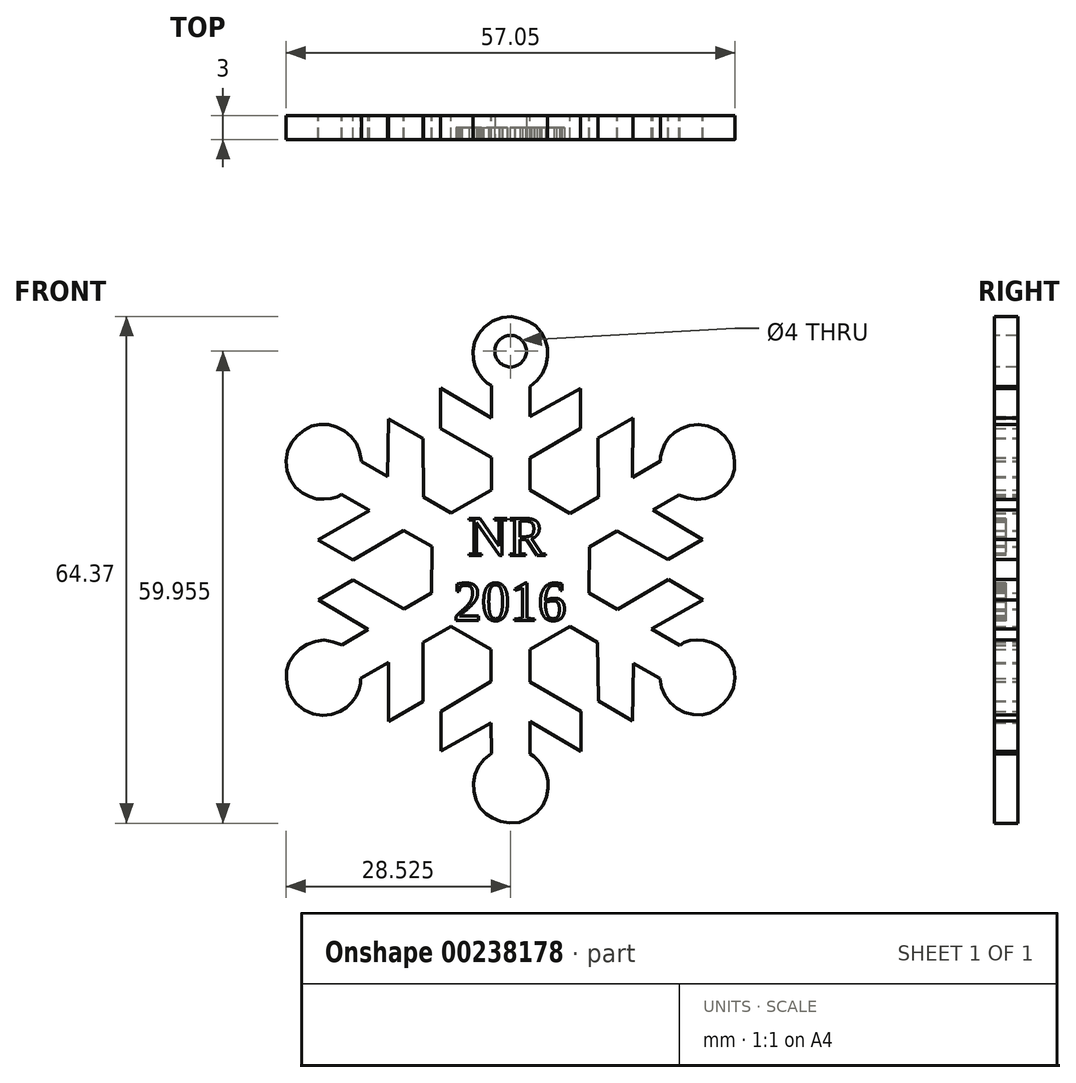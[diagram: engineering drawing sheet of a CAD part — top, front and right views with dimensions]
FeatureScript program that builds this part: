
annotation { "Feature Type Name" : "Feature", "Feature Type Description" : "" }
export const myFeature = defineFeature(function(context is Context, id is Id, definition is map)
    precondition{}
    {
        {
            var Q0;
            Q0=qCreatedBy(makeId("Front.planeOp"),FACE);
            var sketch = newSketch(context, id + "F0", { "sketchPlane" : qUnion([Q0])});
            skFitSpline(sketch, "E0", {"points": [v(37.24, 9.43) * mm, v(37.81, 9.11) * mm, v(38.63, 8.19) * mm, v(39.3, 6.99) * mm, v(39.56, 5.42) * mm, v(39.13, 3.37) * mm, v(37.49, 1.48) * mm, v(35, 0.65) * mm, v(32.8, 1.18) * mm, v(31.32, 2.12) * mm, v(30.3, 3.9) * mm, v(30.1, 5.9) * mm, v(30.72, 7.91) * mm, v(32.35, 9.53) * mm], "startDerivative": vector(12.25, -5.47) * mm, "endDerivative": vector(21.42, 17.4) * mm});
            skFitSpline(sketch, "E1", {"points": [v(32.35, 56.24) * mm, v(31.78, 56.56) * mm, v(30.95, 57.49) * mm, v(30.28, 58.69) * mm, v(30.03, 60.26) * mm, v(30.45, 62.3) * mm, v(32.1, 64.2) * mm, v(34.6, 65.02) * mm, v(36.8, 64.5) * mm, v(38.26, 63.55) * mm, v(39.29, 61.78) * mm, v(39.49, 59.78) * mm, v(38.86, 57.76) * mm, v(37.24, 56.14) * mm], "startDerivative": vector(-12.25, 5.47) * mm, "endDerivative": vector(-21.42, -17.4) * mm});
            skLineSegment(sketch, "E2", {"start": v(32.35, 56.24) * mm, "end": v(32.35, 52.12) * mm});
            skLineSegment(sketch, "E3", {"start": v(32.35, 52.12) * mm, "end": v(25.87, 55.93) * mm});
            skLineSegment(sketch, "E4", {"start": v(25.87, 55.93) * mm, "end": v(25.87, 50.81) * mm});
            skLineSegment(sketch, "E5", {"start": v(25.87, 50.81) * mm, "end": v(32.35, 47.1) * mm});
            skLineSegment(sketch, "E6", {"start": v(32.35, 47.1) * mm, "end": v(32.35, 42.96) * mm});
            skLineSegment(sketch, "E7", {"start": v(37.27, 42.98) * mm, "end": v(37.27, 47.04) * mm});
            skLineSegment(sketch, "E8", {"start": v(37.27, 47.04) * mm, "end": v(43.65, 50.81) * mm});
            skLineSegment(sketch, "E9", {"start": v(43.65, 50.81) * mm, "end": v(43.65, 55.86) * mm});
            skLineSegment(sketch, "E10", {"start": v(43.65, 55.86) * mm, "end": v(37.27, 52.3) * mm});
            skLineSegment(sketch, "E11", {"start": v(37.27, 52.3) * mm, "end": v(37.24, 56.14) * mm});
            skLineSegment(sketch, "E12", {"start": v(27.25, 40.05) * mm, "end": v(32.35, 42.96) * mm});
            skLineSegment(sketch, "E13.1.0", {"start": v(21.21, 37.86) * mm, "end": v(24.8, 35.78) * mm});
            skLineSegment(sketch, "E13.1.1", {"start": v(27.25, 40.05) * mm, "end": v(23.73, 42.08) * mm});
            skLineSegment(sketch, "E13.1.2", {"start": v(24.78, 29.9) * mm, "end": v(24.8, 35.78) * mm});
            skLineSegment(sketch, "E13.1.3", {"start": v(14.76, 34.1) * mm, "end": v(21.21, 37.86) * mm});
            skLineSegment(sketch, "E13.1.4", {"start": v(23.73, 42.08) * mm, "end": v(23.66, 49.5) * mm});
            skLineSegment(sketch, "E13.1.5", {"start": v(23.66, 49.5) * mm, "end": v(19.29, 52.02) * mm});
            skLineSegment(sketch, "E13.1.6", {"start": v(19.29, 52.02) * mm, "end": v(19.18, 44.7) * mm});
            skLineSegment(sketch, "E13.1.7", {"start": v(19.18, 44.7) * mm, "end": v(15.84, 46.6) * mm});
            skLineSegment(sketch, "E13.1.8", {"start": v(13.3, 42.42) * mm, "end": v(16.87, 40.36) * mm});
            skLineSegment(sketch, "E13.1.9", {"start": v(16.87, 40.36) * mm, "end": v(10.33, 36.65) * mm});
            skLineSegment(sketch, "E13.1.10", {"start": v(10.33, 36.65) * mm, "end": v(14.76, 34.1) * mm});
            skLineSegment(sketch, "E13.2.0", {"start": v(23.66, 23.59) * mm, "end": v(27.25, 25.66) * mm});
            skLineSegment(sketch, "E13.2.1", {"start": v(24.78, 29.9) * mm, "end": v(21.26, 27.88) * mm});
            skLineSegment(sketch, "E13.2.2", {"start": v(32.32, 22.7) * mm, "end": v(27.25, 25.66) * mm});
            skLineSegment(sketch, "E13.2.3", {"start": v(23.7, 16.12) * mm, "end": v(23.66, 23.59) * mm});
            skLineSegment(sketch, "E13.2.4", {"start": v(21.26, 27.88) * mm, "end": v(14.8, 31.52) * mm});
            skLineSegment(sketch, "E13.2.5", {"start": v(14.8, 31.52) * mm, "end": v(10.43, 29) * mm});
            skLineSegment(sketch, "E13.2.6", {"start": v(10.43, 29) * mm, "end": v(16.7, 25.25) * mm});
            skLineSegment(sketch, "E13.2.7", {"start": v(16.7, 25.25) * mm, "end": v(13.39, 23.3) * mm});
            skLineSegment(sketch, "E13.2.8", {"start": v(15.75, 19.02) * mm, "end": v(19.32, 21.08) * mm});
            skLineSegment(sketch, "E13.2.9", {"start": v(19.32, 21.08) * mm, "end": v(19.26, 13.56) * mm});
            skLineSegment(sketch, "E13.2.10", {"start": v(19.26, 13.56) * mm, "end": v(23.7, 16.12) * mm});
            skLineSegment(sketch, "E13.3.0", {"start": v(37.24, 18.57) * mm, "end": v(37.24, 22.71) * mm});
            skLineSegment(sketch, "E13.3.1", {"start": v(32.32, 22.7) * mm, "end": v(32.32, 18.64) * mm});
            skLineSegment(sketch, "E13.3.2", {"start": v(42.34, 25.63) * mm, "end": v(37.24, 22.71) * mm});
            skLineSegment(sketch, "E13.3.3", {"start": v(43.72, 14.86) * mm, "end": v(37.24, 18.57) * mm});
            skLineSegment(sketch, "E13.3.4", {"start": v(32.32, 18.64) * mm, "end": v(25.93, 14.86) * mm});
            skLineSegment(sketch, "E13.3.5", {"start": v(25.93, 14.86) * mm, "end": v(25.93, 9.82) * mm});
            skLineSegment(sketch, "E13.3.6", {"start": v(25.93, 9.82) * mm, "end": v(32.32, 13.38) * mm});
            skLineSegment(sketch, "E13.3.7", {"start": v(32.32, 13.38) * mm, "end": v(32.35, 9.53) * mm});
            skLineSegment(sketch, "E13.3.8", {"start": v(37.24, 9.43) * mm, "end": v(37.24, 13.56) * mm});
            skLineSegment(sketch, "E13.3.9", {"start": v(37.24, 13.56) * mm, "end": v(43.72, 9.75) * mm});
            skLineSegment(sketch, "E13.3.10", {"start": v(43.72, 9.75) * mm, "end": v(43.72, 14.86) * mm});
            skLineSegment(sketch, "E13.4.0", {"start": v(48.37, 27.82) * mm, "end": v(44.78, 29.9) * mm});
            skLineSegment(sketch, "E13.4.1", {"start": v(42.34, 25.63) * mm, "end": v(45.85, 23.6) * mm});
            skLineSegment(sketch, "E13.4.2", {"start": v(44.81, 35.77) * mm, "end": v(44.78, 29.9) * mm});
            skLineSegment(sketch, "E13.4.3", {"start": v(54.82, 31.58) * mm, "end": v(48.37, 27.82) * mm});
            skLineSegment(sketch, "E13.4.4", {"start": v(45.85, 23.6) * mm, "end": v(45.93, 16.18) * mm});
            skLineSegment(sketch, "E13.4.5", {"start": v(45.93, 16.18) * mm, "end": v(50.3, 13.65) * mm});
            skLineSegment(sketch, "E13.4.6", {"start": v(50.3, 13.65) * mm, "end": v(50.4, 20.97) * mm});
            skLineSegment(sketch, "E13.4.7", {"start": v(50.4, 20.97) * mm, "end": v(53.75, 19.07) * mm});
            skLineSegment(sketch, "E13.4.8", {"start": v(56.28, 23.25) * mm, "end": v(52.71, 25.31) * mm});
            skLineSegment(sketch, "E13.4.9", {"start": v(52.71, 25.31) * mm, "end": v(59.25, 29.02) * mm});
            skLineSegment(sketch, "E13.4.10", {"start": v(59.25, 29.02) * mm, "end": v(54.82, 31.58) * mm});
            skLineSegment(sketch, "E13.5.0", {"start": v(45.93, 42.09) * mm, "end": v(42.34, 40.02) * mm});
            skLineSegment(sketch, "E13.5.1", {"start": v(44.81, 35.77) * mm, "end": v(48.33, 37.8) * mm});
            skLineSegment(sketch, "E13.5.2", {"start": v(37.27, 42.98) * mm, "end": v(42.34, 40.02) * mm});
            skLineSegment(sketch, "E13.5.3", {"start": v(45.9, 49.55) * mm, "end": v(45.93, 42.09) * mm});
            skLineSegment(sketch, "E13.5.4", {"start": v(48.33, 37.8) * mm, "end": v(54.79, 34.15) * mm});
            skLineSegment(sketch, "E13.5.5", {"start": v(54.79, 34.15) * mm, "end": v(59.16, 36.67) * mm});
            skLineSegment(sketch, "E13.5.6", {"start": v(59.16, 36.67) * mm, "end": v(52.88, 40.42) * mm});
            skLineSegment(sketch, "E13.5.7", {"start": v(52.88, 40.42) * mm, "end": v(56.2, 42.37) * mm});
            skLineSegment(sketch, "E13.5.8", {"start": v(53.84, 46.66) * mm, "end": v(50.27, 44.6) * mm});
            skLineSegment(sketch, "E13.5.9", {"start": v(50.27, 44.6) * mm, "end": v(50.33, 52.11) * mm});
            skLineSegment(sketch, "E13.5.10", {"start": v(50.33, 52.11) * mm, "end": v(45.9, 49.55) * mm});
            skPoint(sketch, "E13.center", {"position": v(34.8, 32.84) * mm});
            skFitSpline(sketch, "E14", {"points": [v(15.75, 19.02) * mm, v(15.74, 18.36) * mm, v(15.35, 17.18) * mm, v(14.65, 16) * mm, v(13.41, 15) * mm, v(11.43, 14.34) * mm, v(8.96, 14.82) * mm, v(7, 16.57) * mm, v(6.36, 18.74) * mm, v(6.44, 20.48) * mm, v(7.46, 22.26) * mm, v(9.1, 23.43) * mm, v(11.16, 23.9) * mm, v(13.39, 23.3) * mm], "startDerivative": vector(1.38, -13.34) * mm, "endDerivative": vector(25.78, -9.85) * mm});
            skFitSpline(sketch, "E15", {"points": [v(56.28, 23.25) * mm, v(56.86, 23.64) * mm, v(58.07, 23.9) * mm, v(59.44, 23.88) * mm, v(60.93, 23.3) * mm, v(62.49, 21.91) * mm, v(63.3, 19.54) * mm, v(62.77, 16.97) * mm, v(61.22, 15.33) * mm, v(59.66, 14.53) * mm, v(57.62, 14.53) * mm, v(55.8, 15.35) * mm, v(54.35, 16.9) * mm, v(53.75, 19.07) * mm], "startDerivative": vector(10.86, 7.87) * mm, "endDerivative": vector(-4.36, 27.26) * mm});
            skFitSpline(sketch, "E16", {"points": [v(13.3, 42.42) * mm, v(12.73, 42.1) * mm, v(11.52, 41.85) * mm, v(10.14, 41.86) * mm, v(8.66, 42.43) * mm, v(7.1, 43.82) * mm, v(6.28, 46.2) * mm, v(6.81, 48.77) * mm, v(8.37, 50.4) * mm, v(9.92, 51.21) * mm, v(11.97, 51.21) * mm, v(13.8, 50.39) * mm, v(15.24, 48.83) * mm, v(15.84, 46.6) * mm], "startDerivative": vector(-10.86, -7.87) * mm, "endDerivative": vector(4.36, -27.26) * mm});
            skFitSpline(sketch, "E17", {"points": [v(53.84, 46.66) * mm, v(53.84, 47.28) * mm, v(54.23, 48.46) * mm, v(54.93, 49.64) * mm, v(56.16, 50.64) * mm, v(58.15, 51.3) * mm, v(60.61, 50.82) * mm, v(62.57, 49.07) * mm, v(63.22, 46.9) * mm, v(63.13, 45.16) * mm, v(62.11, 43.39) * mm, v(60.48, 42.21) * mm, v(58.42, 41.74) * mm, v(56.2, 42.37) * mm], "startDerivative": vector(-1.38, 13.34) * mm, "endDerivative": vector(-25.78, 9.85) * mm});
            skSolve(sketch);
        }
        {
            var Q0;
            Q0=makeQuery(id+"F0.imprint","IMPRINT",FACE,{"disambiguationData":[TD([[makeQuery(id+"F0.imprint","IMPRINT",EDGE,{"derivedFrom":sQuery(id+"F0.wireOp",EDGE,"E0")}),-1.0]])]});
            extrude(context, id + "F1", {"entities" : qUnion([Q0]), "depth" : 3 * mm});
        }
        {
            var Q0;
            Q0=makeQuery(id+"F1.opExtrude","CAP_FACE",FACE,{"disambiguationData":[OSD([sQuery(id+"F0.wireOp",EDGE,"E0"),sQuery(id+"F0.wireOp",EDGE,"E1"),sQuery(id+"F0.wireOp",EDGE,"E2"),sQuery(id+"F0.wireOp",EDGE,"E3"),sQuery(id+"F0.wireOp",EDGE,"E4"),sQuery(id+"F0.wireOp",EDGE,"E5"),sQuery(id+"F0.wireOp",EDGE,"E6"),sQuery(id+"F0.wireOp",EDGE,"E7"),sQuery(id+"F0.wireOp",EDGE,"E8"),sQuery(id+"F0.wireOp",EDGE,"E9"),sQuery(id+"F0.wireOp",EDGE,"E10"),sQuery(id+"F0.wireOp",EDGE,"E11"),sQuery(id+"F0.wireOp",EDGE,"E12"),sQuery(id+"F0.wireOp",EDGE,"E13.1.0"),sQuery(id+"F0.wireOp",EDGE,"E13.1.1"),sQuery(id+"F0.wireOp",EDGE,"E13.1.2"),sQuery(id+"F0.wireOp",EDGE,"E13.1.3"),sQuery(id+"F0.wireOp",EDGE,"E13.1.4"),sQuery(id+"F0.wireOp",EDGE,"E13.1.5"),sQuery(id+"F0.wireOp",EDGE,"E13.1.6"),sQuery(id+"F0.wireOp",EDGE,"E13.1.7"),sQuery(id+"F0.wireOp",EDGE,"E13.1.8"),sQuery(id+"F0.wireOp",EDGE,"E13.1.9"),sQuery(id+"F0.wireOp",EDGE,"E13.1.10"),sQuery(id+"F0.wireOp",EDGE,"E13.2.0"),sQuery(id+"F0.wireOp",EDGE,"E13.2.1"),sQuery(id+"F0.wireOp",EDGE,"E13.2.2"),sQuery(id+"F0.wireOp",EDGE,"E13.2.3"),sQuery(id+"F0.wireOp",EDGE,"E13.2.4"),sQuery(id+"F0.wireOp",EDGE,"E13.2.5"),sQuery(id+"F0.wireOp",EDGE,"E13.2.6"),sQuery(id+"F0.wireOp",EDGE,"E13.2.7"),sQuery(id+"F0.wireOp",EDGE,"E13.2.8"),sQuery(id+"F0.wireOp",EDGE,"E13.2.9"),sQuery(id+"F0.wireOp",EDGE,"E13.2.10"),sQuery(id+"F0.wireOp",EDGE,"E13.3.0"),sQuery(id+"F0.wireOp",EDGE,"E13.3.1"),sQuery(id+"F0.wireOp",EDGE,"E13.3.2"),sQuery(id+"F0.wireOp",EDGE,"E13.3.3"),sQuery(id+"F0.wireOp",EDGE,"E13.3.4"),sQuery(id+"F0.wireOp",EDGE,"E13.3.5"),sQuery(id+"F0.wireOp",EDGE,"E13.3.6"),sQuery(id+"F0.wireOp",EDGE,"E13.3.7"),sQuery(id+"F0.wireOp",EDGE,"E13.3.8"),sQuery(id+"F0.wireOp",EDGE,"E13.3.9"),sQuery(id+"F0.wireOp",EDGE,"E13.3.10"),sQuery(id+"F0.wireOp",EDGE,"E13.4.0"),sQuery(id+"F0.wireOp",EDGE,"E13.4.1"),sQuery(id+"F0.wireOp",EDGE,"E13.4.2"),sQuery(id+"F0.wireOp",EDGE,"E13.4.3"),sQuery(id+"F0.wireOp",EDGE,"E13.4.4"),sQuery(id+"F0.wireOp",EDGE,"E13.4.5"),sQuery(id+"F0.wireOp",EDGE,"E13.4.6"),sQuery(id+"F0.wireOp",EDGE,"E13.4.7"),sQuery(id+"F0.wireOp",EDGE,"E13.4.8"),sQuery(id+"F0.wireOp",EDGE,"E13.4.9"),sQuery(id+"F0.wireOp",EDGE,"E13.4.10"),sQuery(id+"F0.wireOp",EDGE,"E13.5.0"),sQuery(id+"F0.wireOp",EDGE,"E13.5.1"),sQuery(id+"F0.wireOp",EDGE,"E13.5.2"),sQuery(id+"F0.wireOp",EDGE,"E13.5.3"),sQuery(id+"F0.wireOp",EDGE,"E13.5.4"),sQuery(id+"F0.wireOp",EDGE,"E13.5.5"),sQuery(id+"F0.wireOp",EDGE,"E13.5.6"),sQuery(id+"F0.wireOp",EDGE,"E13.5.7"),sQuery(id+"F0.wireOp",EDGE,"E13.5.8"),sQuery(id+"F0.wireOp",EDGE,"E13.5.9"),sQuery(id+"F0.wireOp",EDGE,"E13.5.10"),sQuery(id+"F0.wireOp",EDGE,"E14"),sQuery(id+"F0.wireOp",EDGE,"E15"),sQuery(id+"F0.wireOp",EDGE,"E16"),sQuery(id+"F0.wireOp",EDGE,"E17")])],"isStart":false});
            var sketch = newSketch(context, id + "F2", { "sketchPlane" : qUnion([Q0])});
            skCircle(sketch, "E18", {"center": v(34.8, 60.6) * mm, "radius": 2 * mm});
            skSolve(sketch);
        }
        {
            var Q0;
            Q0=sQuery(id+"F2.wireOp",VERTEX,"E18.center");
            var Q1;
            Q1=makeQuery(id+"F1.opExtrude","SWEPT_BODY",BODY,{"disambiguationData":[OSD([sQuery(id+"F0.wireOp",EDGE,"E0"),sQuery(id+"F0.wireOp",EDGE,"E1"),sQuery(id+"F0.wireOp",EDGE,"E2"),sQuery(id+"F0.wireOp",EDGE,"E3"),sQuery(id+"F0.wireOp",EDGE,"E4"),sQuery(id+"F0.wireOp",EDGE,"E5"),sQuery(id+"F0.wireOp",EDGE,"E6"),sQuery(id+"F0.wireOp",EDGE,"E7"),sQuery(id+"F0.wireOp",EDGE,"E8"),sQuery(id+"F0.wireOp",EDGE,"E9"),sQuery(id+"F0.wireOp",EDGE,"E10"),sQuery(id+"F0.wireOp",EDGE,"E11"),sQuery(id+"F0.wireOp",EDGE,"E12"),sQuery(id+"F0.wireOp",EDGE,"E13.1.0"),sQuery(id+"F0.wireOp",EDGE,"E13.1.1"),sQuery(id+"F0.wireOp",EDGE,"E13.1.2"),sQuery(id+"F0.wireOp",EDGE,"E13.1.3"),sQuery(id+"F0.wireOp",EDGE,"E13.1.4"),sQuery(id+"F0.wireOp",EDGE,"E13.1.5"),sQuery(id+"F0.wireOp",EDGE,"E13.1.6"),sQuery(id+"F0.wireOp",EDGE,"E13.1.7"),sQuery(id+"F0.wireOp",EDGE,"E13.1.8"),sQuery(id+"F0.wireOp",EDGE,"E13.1.9"),sQuery(id+"F0.wireOp",EDGE,"E13.1.10"),sQuery(id+"F0.wireOp",EDGE,"E13.2.0"),sQuery(id+"F0.wireOp",EDGE,"E13.2.1"),sQuery(id+"F0.wireOp",EDGE,"E13.2.2"),sQuery(id+"F0.wireOp",EDGE,"E13.2.3"),sQuery(id+"F0.wireOp",EDGE,"E13.2.4"),sQuery(id+"F0.wireOp",EDGE,"E13.2.5"),sQuery(id+"F0.wireOp",EDGE,"E13.2.6"),sQuery(id+"F0.wireOp",EDGE,"E13.2.7"),sQuery(id+"F0.wireOp",EDGE,"E13.2.8"),sQuery(id+"F0.wireOp",EDGE,"E13.2.9"),sQuery(id+"F0.wireOp",EDGE,"E13.2.10"),sQuery(id+"F0.wireOp",EDGE,"E13.3.0"),sQuery(id+"F0.wireOp",EDGE,"E13.3.1"),sQuery(id+"F0.wireOp",EDGE,"E13.3.2"),sQuery(id+"F0.wireOp",EDGE,"E13.3.3"),sQuery(id+"F0.wireOp",EDGE,"E13.3.4"),sQuery(id+"F0.wireOp",EDGE,"E13.3.5"),sQuery(id+"F0.wireOp",EDGE,"E13.3.6"),sQuery(id+"F0.wireOp",EDGE,"E13.3.7"),sQuery(id+"F0.wireOp",EDGE,"E13.3.8"),sQuery(id+"F0.wireOp",EDGE,"E13.3.9"),sQuery(id+"F0.wireOp",EDGE,"E13.3.10"),sQuery(id+"F0.wireOp",EDGE,"E13.4.0"),sQuery(id+"F0.wireOp",EDGE,"E13.4.1"),sQuery(id+"F0.wireOp",EDGE,"E13.4.2"),sQuery(id+"F0.wireOp",EDGE,"E13.4.3"),sQuery(id+"F0.wireOp",EDGE,"E13.4.4"),sQuery(id+"F0.wireOp",EDGE,"E13.4.5"),sQuery(id+"F0.wireOp",EDGE,"E13.4.6"),sQuery(id+"F0.wireOp",EDGE,"E13.4.7"),sQuery(id+"F0.wireOp",EDGE,"E13.4.8"),sQuery(id+"F0.wireOp",EDGE,"E13.4.9"),sQuery(id+"F0.wireOp",EDGE,"E13.4.10"),sQuery(id+"F0.wireOp",EDGE,"E13.5.0"),sQuery(id+"F0.wireOp",EDGE,"E13.5.1"),sQuery(id+"F0.wireOp",EDGE,"E13.5.2"),sQuery(id+"F0.wireOp",EDGE,"E13.5.3"),sQuery(id+"F0.wireOp",EDGE,"E13.5.4"),sQuery(id+"F0.wireOp",EDGE,"E13.5.5"),sQuery(id+"F0.wireOp",EDGE,"E13.5.6"),sQuery(id+"F0.wireOp",EDGE,"E13.5.7"),sQuery(id+"F0.wireOp",EDGE,"E13.5.8"),sQuery(id+"F0.wireOp",EDGE,"E13.5.9"),sQuery(id+"F0.wireOp",EDGE,"E13.5.10"),sQuery(id+"F0.wireOp",EDGE,"E14"),sQuery(id+"F0.wireOp",EDGE,"E15"),sQuery(id+"F0.wireOp",EDGE,"E16"),sQuery(id+"F0.wireOp",EDGE,"E17")])]});
            hole(context, id + "F3", {"style" : HoleStyle.SIMPLE, "endStyle" : HoleEndStyle.THROUGH, "holeDiameter" : 4 * mm, "isTappedThrough" : true, "tappedDepth" : 12 * mm, "tapClearance" : 3, "locations" : qUnion([Q0]), "scope" : qUnion([Q1])});
        }
        {
            var Q0;
            Q0=makeQuery(id+"F1.opExtrude","CAP_FACE",FACE,{"disambiguationData":[OSD([sQuery(id+"F0.wireOp",EDGE,"E0"),sQuery(id+"F0.wireOp",EDGE,"E1"),sQuery(id+"F0.wireOp",EDGE,"E2"),sQuery(id+"F0.wireOp",EDGE,"E3"),sQuery(id+"F0.wireOp",EDGE,"E4"),sQuery(id+"F0.wireOp",EDGE,"E5"),sQuery(id+"F0.wireOp",EDGE,"E6"),sQuery(id+"F0.wireOp",EDGE,"E7"),sQuery(id+"F0.wireOp",EDGE,"E8"),sQuery(id+"F0.wireOp",EDGE,"E9"),sQuery(id+"F0.wireOp",EDGE,"E10"),sQuery(id+"F0.wireOp",EDGE,"E11"),sQuery(id+"F0.wireOp",EDGE,"E12"),sQuery(id+"F0.wireOp",EDGE,"E13.1.0"),sQuery(id+"F0.wireOp",EDGE,"E13.1.1"),sQuery(id+"F0.wireOp",EDGE,"E13.1.2"),sQuery(id+"F0.wireOp",EDGE,"E13.1.3"),sQuery(id+"F0.wireOp",EDGE,"E13.1.4"),sQuery(id+"F0.wireOp",EDGE,"E13.1.5"),sQuery(id+"F0.wireOp",EDGE,"E13.1.6"),sQuery(id+"F0.wireOp",EDGE,"E13.1.7"),sQuery(id+"F0.wireOp",EDGE,"E13.1.8"),sQuery(id+"F0.wireOp",EDGE,"E13.1.9"),sQuery(id+"F0.wireOp",EDGE,"E13.1.10"),sQuery(id+"F0.wireOp",EDGE,"E13.2.0"),sQuery(id+"F0.wireOp",EDGE,"E13.2.1"),sQuery(id+"F0.wireOp",EDGE,"E13.2.2"),sQuery(id+"F0.wireOp",EDGE,"E13.2.3"),sQuery(id+"F0.wireOp",EDGE,"E13.2.4"),sQuery(id+"F0.wireOp",EDGE,"E13.2.5"),sQuery(id+"F0.wireOp",EDGE,"E13.2.6"),sQuery(id+"F0.wireOp",EDGE,"E13.2.7"),sQuery(id+"F0.wireOp",EDGE,"E13.2.8"),sQuery(id+"F0.wireOp",EDGE,"E13.2.9"),sQuery(id+"F0.wireOp",EDGE,"E13.2.10"),sQuery(id+"F0.wireOp",EDGE,"E13.3.0"),sQuery(id+"F0.wireOp",EDGE,"E13.3.1"),sQuery(id+"F0.wireOp",EDGE,"E13.3.2"),sQuery(id+"F0.wireOp",EDGE,"E13.3.3"),sQuery(id+"F0.wireOp",EDGE,"E13.3.4"),sQuery(id+"F0.wireOp",EDGE,"E13.3.5"),sQuery(id+"F0.wireOp",EDGE,"E13.3.6"),sQuery(id+"F0.wireOp",EDGE,"E13.3.7"),sQuery(id+"F0.wireOp",EDGE,"E13.3.8"),sQuery(id+"F0.wireOp",EDGE,"E13.3.9"),sQuery(id+"F0.wireOp",EDGE,"E13.3.10"),sQuery(id+"F0.wireOp",EDGE,"E13.4.0"),sQuery(id+"F0.wireOp",EDGE,"E13.4.1"),sQuery(id+"F0.wireOp",EDGE,"E13.4.2"),sQuery(id+"F0.wireOp",EDGE,"E13.4.3"),sQuery(id+"F0.wireOp",EDGE,"E13.4.4"),sQuery(id+"F0.wireOp",EDGE,"E13.4.5"),sQuery(id+"F0.wireOp",EDGE,"E13.4.6"),sQuery(id+"F0.wireOp",EDGE,"E13.4.7"),sQuery(id+"F0.wireOp",EDGE,"E13.4.8"),sQuery(id+"F0.wireOp",EDGE,"E13.4.9"),sQuery(id+"F0.wireOp",EDGE,"E13.4.10"),sQuery(id+"F0.wireOp",EDGE,"E13.5.0"),sQuery(id+"F0.wireOp",EDGE,"E13.5.1"),sQuery(id+"F0.wireOp",EDGE,"E13.5.2"),sQuery(id+"F0.wireOp",EDGE,"E13.5.3"),sQuery(id+"F0.wireOp",EDGE,"E13.5.4"),sQuery(id+"F0.wireOp",EDGE,"E13.5.5"),sQuery(id+"F0.wireOp",EDGE,"E13.5.6"),sQuery(id+"F0.wireOp",EDGE,"E13.5.7"),sQuery(id+"F0.wireOp",EDGE,"E13.5.8"),sQuery(id+"F0.wireOp",EDGE,"E13.5.9"),sQuery(id+"F0.wireOp",EDGE,"E13.5.10"),sQuery(id+"F0.wireOp",EDGE,"E14"),sQuery(id+"F0.wireOp",EDGE,"E15"),sQuery(id+"F0.wireOp",EDGE,"E16"),sQuery(id+"F0.wireOp",EDGE,"E17")])],"isStart":false});
            var sketch = newSketch(context, id + "F4", { "sketchPlane" : qUnion([Q0])});
            skPoint(sketch, "E19", {"position": v(34.84, 32.8) * mm});
            skText(sketch, "E20", { "text": " NR\n2016", "fontName": "Tinos-Regular.ttf"});
            const initialGuessF4  = {"E20": [0.02752, 0.03466, 1, 0, 0.00516]};
            skSetInitialGuess(sketch, initialGuessF4);
            skSolve(sketch);
        }
        {
            var Q0;
            Q0=makeQuery(id+"F4.imprint","IMPRINT",FACE,{"disambiguationData":[TD([[makeQuery(id+"F4.imprint","IMPRINT",EDGE,{"derivedFrom":sQuery(id+"F4.wireOp",EDGE,"E20.sketch_text.stroke-0")}),-1.0]])]});
            var Q1;
            Q1=makeQuery(id+"F4.imprint","IMPRINT",FACE,{"disambiguationData":[TD([[makeQuery(id+"F4.imprint","IMPRINT",EDGE,{"derivedFrom":sQuery(id+"F4.wireOp",EDGE,"E20.sketch_text.stroke-22")}),-1.0]])]});
            var Q2;
            Q2=makeQuery(id+"F4.imprint","IMPRINT",FACE,{"disambiguationData":[TD([[makeQuery(id+"F4.imprint","IMPRINT",EDGE,{"derivedFrom":sQuery(id+"F4.wireOp",EDGE,"E20.sketch_text.stroke-37")}),-1.0]])]});
            var Q3;
            Q3=makeQuery(id+"F4.imprint","IMPRINT",FACE,{"disambiguationData":[TD([[makeQuery(id+"F4.imprint","IMPRINT",EDGE,{"derivedFrom":sQuery(id+"F4.wireOp",EDGE,"E20.sketch_text.stroke-48")}),-1.0]])]});
            var Q4;
            Q4=makeQuery(id+"F4.imprint","IMPRINT",FACE,{"disambiguationData":[TD([[makeQuery(id+"F4.imprint","IMPRINT",EDGE,{"derivedFrom":sQuery(id+"F4.wireOp",EDGE,"E20.sketch_text.stroke-49")}),-1.0]])]});
            var Q5;
            Q5=makeQuery(id+"F4.imprint","IMPRINT",FACE,{"disambiguationData":[TD([[makeQuery(id+"F4.imprint","IMPRINT",EDGE,{"derivedFrom":sQuery(id+"F4.wireOp",EDGE,"E20.sketch_text.stroke-71")}),-1.0]])]});
            var Q6;
            Q6=makeQuery(id+"F4.imprint","IMPRINT",FACE,{"disambiguationData":[TD([[makeQuery(id+"F4.imprint","IMPRINT",EDGE,{"derivedFrom":sQuery(id+"F4.wireOp",EDGE,"E20.sketch_text.stroke-86")}),-1.0]])]});
            var Q7;
            Q7=makeQuery(id+"F4.imprint","IMPRINT",FACE,{"disambiguationData":[TD([[makeQuery(id+"F4.imprint","IMPRINT",EDGE,{"derivedFrom":sQuery(id+"F4.wireOp",EDGE,"E20.sketch_text.stroke-97")}),-1.0]])]});
            extrude(context, id + "F5", {"entities" : qUnion([Q0, Q1, Q2, Q3, Q4, Q5, Q6, Q7]), "operationType" : NewBodyOperationType.REMOVE, "oppositeDirection" : true, "depth" : 1.5 * mm});
        }
    });
